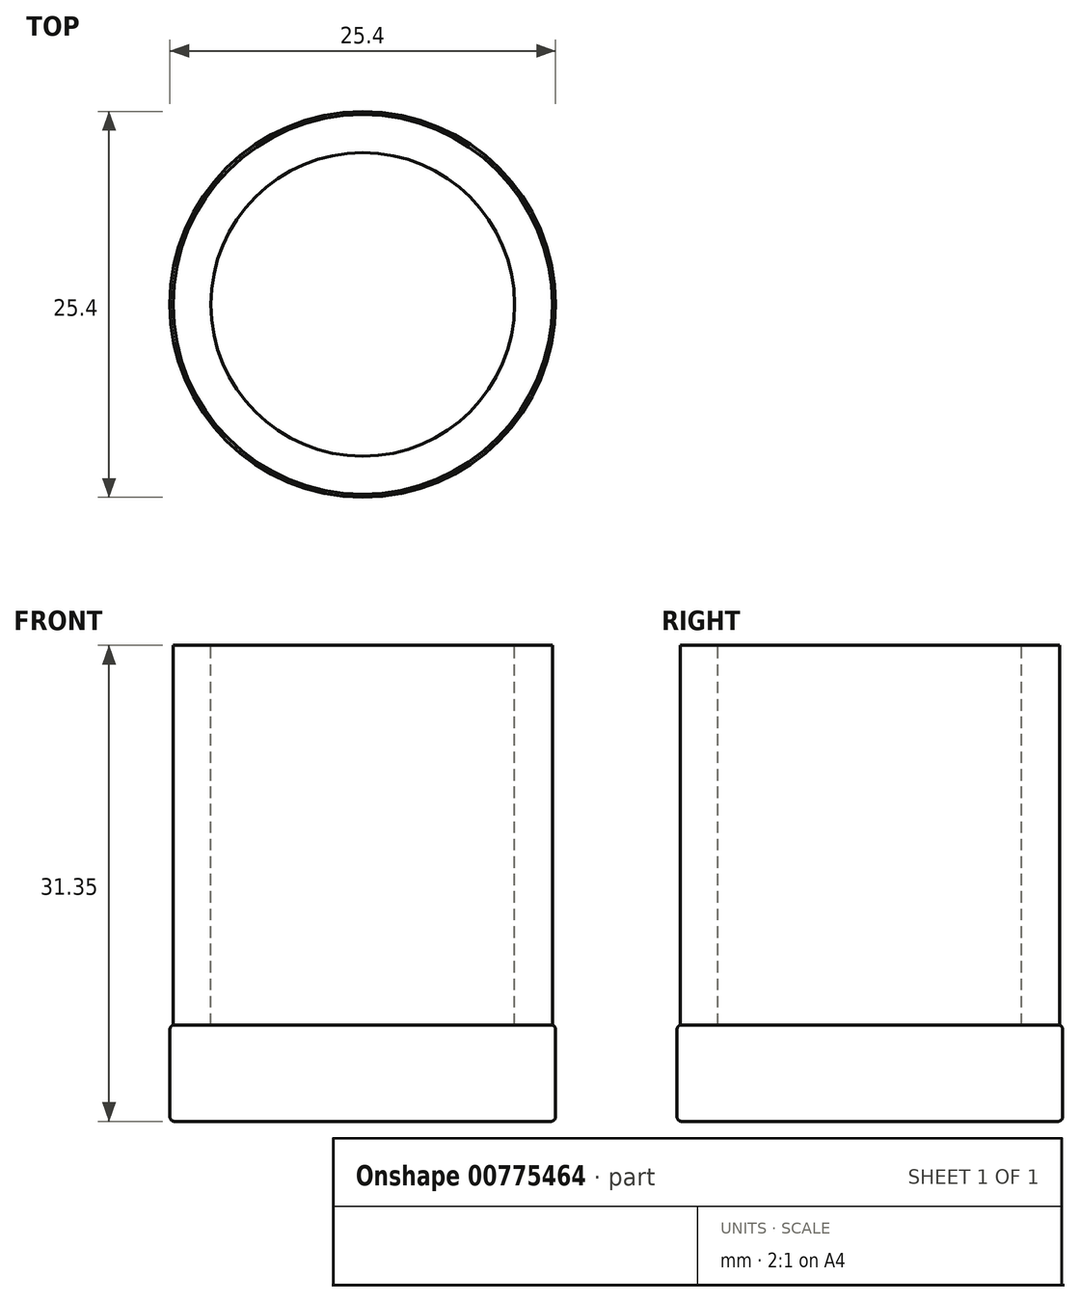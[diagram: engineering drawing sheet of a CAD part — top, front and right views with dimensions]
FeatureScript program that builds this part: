
annotation { "Feature Type Name" : "Feature", "Feature Type Description" : "" }
export const myFeature = defineFeature(function(context is Context, id is Id, definition is map)
    precondition{}
    {
        {
            var Q0;
            Q0=qCreatedBy(makeId("Front.planeOp"),FACE);
            var sketch = newSketch(context, id + "F0", { "sketchPlane" : qUnion([Q0])});
            skLineSegment(sketch, "E0", {"start": v(0, 0) * mm, "end": v(10, 0) * mm, "construction": true});
            skLineSegment(sketch, "E1", {"start": v(10, 0) * mm, "end": v(12.5, 0) * mm, "construction": true});
            skLineSegment(sketch, "E2", {"start": v(0, 0) * mm, "end": v(0, 12.5) * mm, "construction": true});
            skLineSegment(sketch, "E3", {"start": v(10, 12.5) * mm, "end": v(0, 12.5) * mm, "construction": true});
            skLineSegment(sketch, "E4", {"start": v(0, 12.5) * mm, "end": v(0, -12.5) * mm, "construction": true});
            skLineSegment(sketch, "E5", {"start": v(0, -12.5) * mm, "end": v(12.5, -12.5) * mm, "construction": true});
            skLineSegment(sketch, "E6", {"start": v(12.5, -12.5) * mm, "end": v(12.5, 12.5) * mm, "construction": true});
            skLineSegment(sketch, "E7", {"start": v(12.5, 12.5) * mm, "end": v(10, 12.5) * mm, "construction": true});
            skLineSegment(sketch, "E8", {"start": v(10, 12.5) * mm, "end": v(10, -12.5) * mm, "construction": true});
            skLineSegment(sketch, "E9.bottom", {"start": v(10, 12.5) * mm, "end": v(12.5, 12.5) * mm});
            skLineSegment(sketch, "E9.top", {"start": v(10, -12.5) * mm, "end": v(12.5, -12.5) * mm});
            skLineSegment(sketch, "E9.left", {"start": v(10, 12.5) * mm, "end": v(10, -12.5) * mm});
            skLineSegment(sketch, "E9.right", {"start": v(12.5, 12.5) * mm, "end": v(12.5, -12.5) * mm});
            skLineSegment(sketch, "E10.bottom", {"start": v(0, -12.5) * mm, "end": v(12.4, -12.5) * mm});
            skLineSegment(sketch, "E10.top", {"start": v(0, -18.85) * mm, "end": v(12.4, -18.85) * mm});
            skLineSegment(sketch, "E10.left", {"start": v(0, -12.5) * mm, "end": v(0, -18.85) * mm});
            skLineSegment(sketch, "E10.right", {"start": v(12.7, -12.8) * mm, "end": v(12.7, -18.55) * mm});
            skPoint(sketch, "E11.visualSharp", {"position": v(12.7, -12.5) * mm});
            skArc(sketch, "E11.filletArc", {"start": v(12.7, -12.8) * mm, "mid": v(12.61, -12.59) * mm, "end": v(12.4, -12.5) * mm});
            skPoint(sketch, "E12.visualSharp", {"position": v(12.7, -18.85) * mm});
            skArc(sketch, "E12.filletArc", {"start": v(12.4, -18.85) * mm, "mid": v(12.61, -18.76) * mm, "end": v(12.7, -18.55) * mm});
            skSolve(sketch);
        }
        {
            var Q0;
            Q0=makeQuery(id+"F0.imprint","IMPRINT",FACE,{"disambiguationData":[TD([[makeQuery(id+"F0.imprint","IMPRINT",EDGE,{"derivedFrom":sQuery(id+"F0.wireOp",EDGE,"E9.bottom")}),-1.0]])]});
            var Q1;
            Q1=sQuery(id+"F0.wireOp",EDGE,"E4");
            revolve(context, id + "F1", {"surfaceOperationType" : NewSurfaceOperationType.NEW, "entities" : qUnion([Q0]), "axis" : qUnion([Q1]), "revolveType" : RevolveType.FULL});
        }
        {
            var Q0;
            Q0=qCreatedBy(makeId("Right.planeOp"),FACE);
            cPlane(context, id + "F2", {"entities" : qUnion([Q0]), "cplaneType" : CPlaneType.OFFSET, "offset" : 10 * mm, "width" : 150 * mm, "height" : 150 * mm});
        }
        {
            var Q0;
            Q0=makeQuery(id+"F0.imprint","IMPRINT",FACE,{"disambiguationData":[TD([[makeQuery(id+"F0.imprint","IMPRINT",EDGE,{"derivedFrom":sQuery(id+"F0.wireOp",EDGE,"E10.top")}),1.0]])]});
            var Q1;
            Q1=sQuery(id+"F0.wireOp",EDGE,"E10.left");
            revolve(context, id + "F3", {"surfaceOperationType" : NewSurfaceOperationType.NEW, "entities" : qUnion([Q0]), "axis" : qUnion([Q1]), "revolveType" : RevolveType.FULL});
        }
    });
